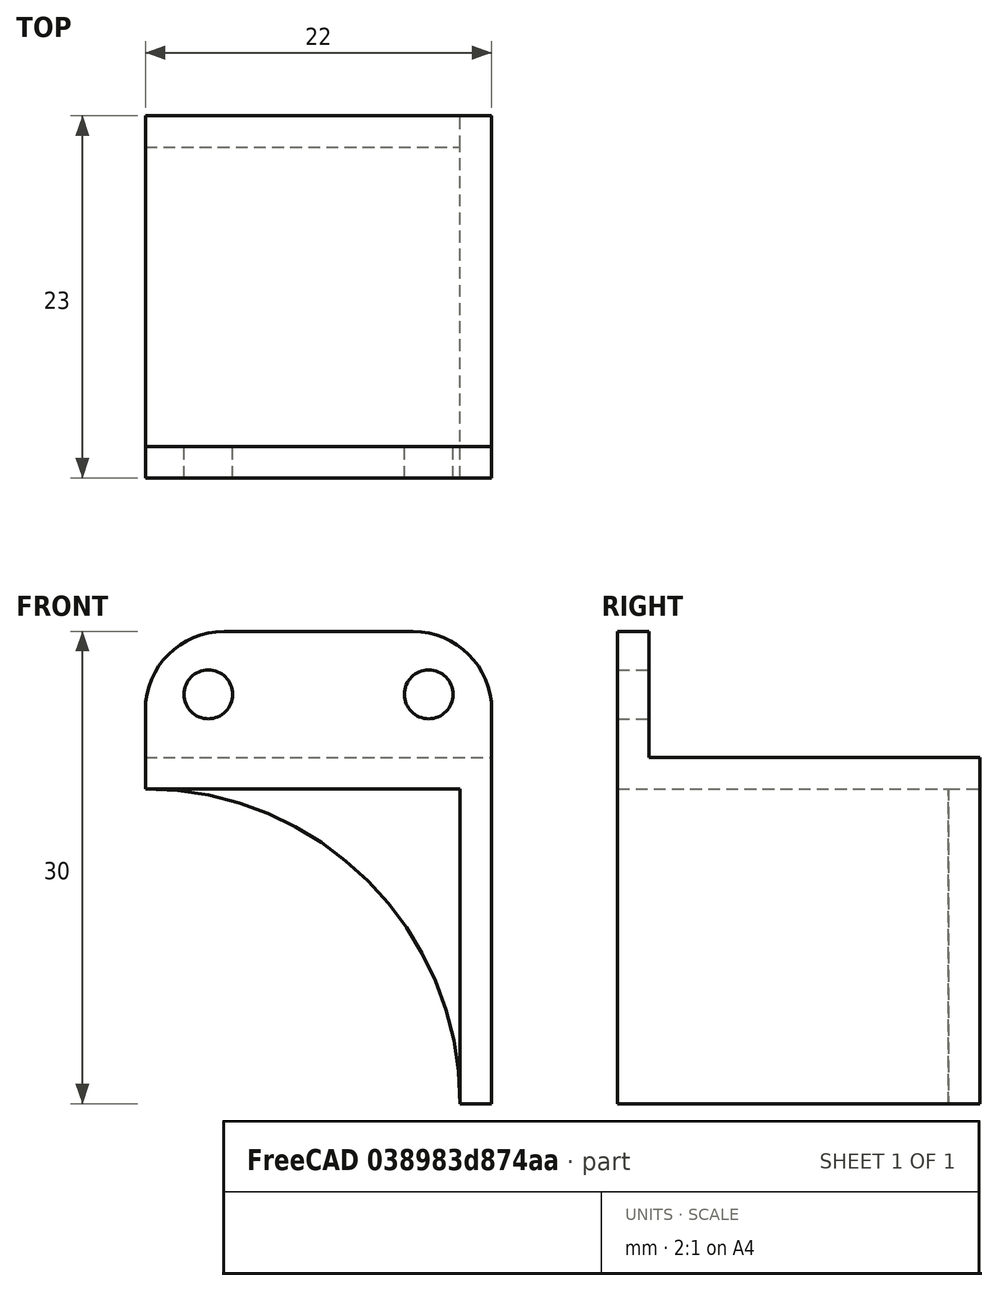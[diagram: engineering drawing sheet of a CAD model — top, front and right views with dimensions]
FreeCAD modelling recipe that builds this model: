
FCSTD DOCUMENT  (FreeCAD 0.17R13541 (Git))
Label: sujetador-left
License: All rights reserved
LicenseURL: http://en.wikipedia.org/wiki/All_rights_reserved
objects: Part::Cut×5, Part::Box×4, Part::Cylinder×3, Part::Fillet×2, Part::MultiFuse×1
note: 15 computed .brp shape members not serialized (recipe doc carries the construction recipe); baked Part::Feature solids carry a one-line shape summary decoded from their .brp

FEATURE [Part::Box] Box  label="Cubo"
  AttacherType = Attacher::AttachEngine3D
  Height = 22
  Length = 22
  Width = 23
FEATURE [Part::Box] Box001  label="Cubo001"
  AttacherType = Attacher::AttachEngine3D
  Height = 20
  Length = 20
  Width = 21
FEATURE [Part::Box] Box002  label="Cubo002"
  AttacherType = Attacher::AttachEngine3D
  Height = 30
  Length = 30
  Width = 2
FEATURE [Part::Cylinder] Cylinder  label="Cilindro"
  Angle = 360
  AttacherType = Attacher::AttachEngine3D
  Height = 10
  Placement = pos=(18,-2,26) rot=(-1,0,0;1.5708rad)
  Radius = 1.55
FEATURE [Part::Cylinder] Cylinder001  label="Cilindro001"
  Angle = 360
  AttacherType = Attacher::AttachEngine3D
  Height = 25
  Placement = pos=(0,0,0) rot=(-1,0,0;1.5708rad)
  Radius = 20
FEATURE [Part::Cylinder] Cylinder002  label="Cilindro002"
  Angle = 360
  AttacherType = Attacher::AttachEngine3D
  Height = 10
  Placement = pos=(4,-2,26) rot=(-1,0,0;1.5708rad)
  Radius = 1.55
FEATURE [Part::MultiFuse] Fusion
  Refine = true
  Shapes = -> [Box002,Box]
FEATURE [Part::Cut] Cut
  Base = -> Fusion
  Refine = true
  Tool = -> Box001
FEATURE [Part::Box] Box003  label="Cubo003"
  AttacherType = Attacher::AttachEngine3D
  Height = 31
  Length = 10
  Placement = pos=(22,0,0) rot=(0,0,1;0rad)
  Width = 6
FEATURE [Part::Cut] Cut001
  Base = -> Cut
  Refine = true
  Tool = -> Box003
FEATURE [Part::Cut] Cut002
  Base = -> Cut001
  Refine = true
  Tool = -> Cylinder
FEATURE [Part::Cut] Cut003
  Base = -> Cut002
  Refine = true
  Tool = -> Cylinder002
FEATURE [Part::Cut] Cut004
  Base = -> Cut003
  Refine = true
  Tool = -> Cylinder001
FEATURE [Part::Fillet] Fillet
  Base = -> Cut004
  Edges = 1 edges r=5: [Edge4]
FEATURE [Part::Fillet] Fillet001
  Base = -> Fillet
  Edges = 1 edges r=5: [Edge3]
